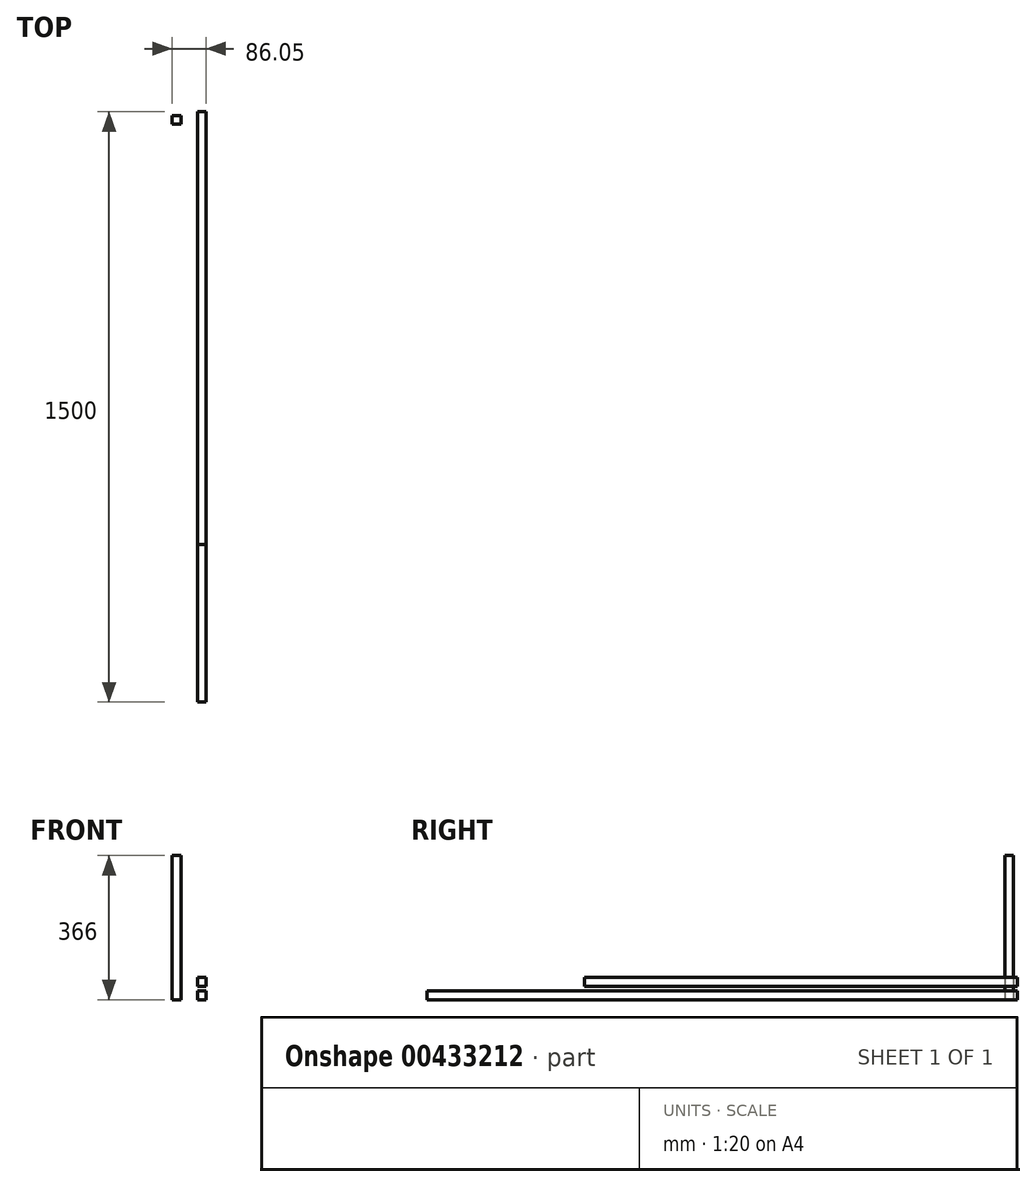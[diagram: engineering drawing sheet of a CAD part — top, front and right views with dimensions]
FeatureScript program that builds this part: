
annotation { "Feature Type Name" : "Feature", "Feature Type Description" : "" }
export const myFeature = defineFeature(function(context is Context, id is Id, definition is map)
    precondition{}
    {
        {
            assignVariable(context, id + "F0", {"name" : "SquareWidth", "anyValue" : 22});
        }
        {
            assignVariable(context, id + "F1", {"name" : "PenHeight", "anyValue" : 410});
        }
        {
            assignVariable(context, id + "F2", {"name" : "VerticalSideHeight", "anyValue" : getVariable(context, 'PenHeight') - getVariable(context, 'SquareWidth') - getVariable(context, 'SquareWidth')});
        }
        {
            var Q0;
            Q0=qCreatedBy(makeId("Front.planeOp"),FACE);
            var sketch = newSketch(context, id + "F3", { "sketchPlane" : qUnion([Q0])});
            skLineSegment(sketch, "E0.bottom", {"start": v(0, 0) * mm, "end": v(22, 0) * mm});
            skLineSegment(sketch, "E0.top", {"start": v(0, 22) * mm, "end": v(22, 22) * mm});
            skLineSegment(sketch, "E0.left", {"start": v(0, 0) * mm, "end": v(0, 22) * mm});
            skLineSegment(sketch, "E0.right", {"start": v(22, 0) * mm, "end": v(22, 22) * mm});
            skSolve(sketch);
        }
        {
            var Q0;
            Q0 = qSketchRegion(id + "F3", true);
            extrude(context, id + "F4", {"entities" : qUnion([Q0]), "depth" : 1500 * mm});
        }
        {
            var Q0;
            Q0=qCreatedBy(makeId("Top.planeOp"),FACE);
            var sketch = newSketch(context, id + "F5", { "sketchPlane" : qUnion([Q0])});
            skLineSegment(sketch, "E1.bottom", {"start": v(-64.05, -9.98) * mm, "end": v(-42.05, -9.98) * mm});
            skLineSegment(sketch, "E1.top", {"start": v(-64.05, -31.98) * mm, "end": v(-42.05, -31.98) * mm});
            skLineSegment(sketch, "E1.left", {"start": v(-64.05, -9.98) * mm, "end": v(-64.05, -31.98) * mm});
            skLineSegment(sketch, "E1.right", {"start": v(-42.05, -9.98) * mm, "end": v(-42.05, -31.98) * mm});
            skSolve(sketch);
        }
        {
            var Q0;
            Q0 = qSketchRegion(id + "F5", true);
            extrude(context, id + "F6", {"entities" : qUnion([Q0]), "depth" : (getVariable(context, 'VerticalSideHeight')) * mm});
        }
        {
            var Q0;
            Q0=qCreatedBy(makeId("Front.planeOp"),FACE);
            var sketch = newSketch(context, id + "F7", { "sketchPlane" : qUnion([Q0])});
            skLineSegment(sketch, "E2.bottom", {"start": v(0, 34.35) * mm, "end": v(22, 34.35) * mm});
            skLineSegment(sketch, "E2.top", {"start": v(0, 56.35) * mm, "end": v(22, 56.35) * mm});
            skLineSegment(sketch, "E2.left", {"start": v(0, 34.35) * mm, "end": v(0, 56.35) * mm});
            skLineSegment(sketch, "E2.right", {"start": v(22, 34.35) * mm, "end": v(22, 56.35) * mm});
            skSolve(sketch);
        }
        {
            var Q0;
            Q0 = qSketchRegion(id + "F7", true);
            extrude(context, id + "F8", {"entities" : qUnion([Q0]), "depth" : 1100 * mm});
        }
    });
